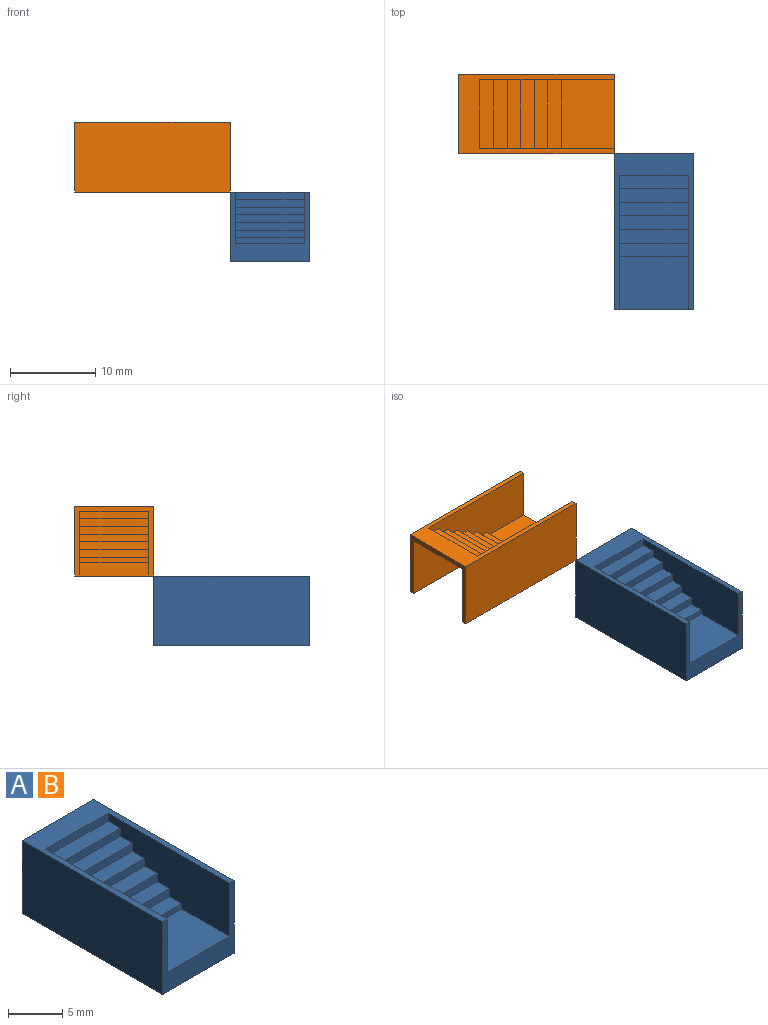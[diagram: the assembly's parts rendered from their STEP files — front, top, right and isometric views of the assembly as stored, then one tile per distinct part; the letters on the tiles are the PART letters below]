
ASSEMBLY  parts=2 mates=1
PART A: 40 faces, bbox 9.3x18.3x8.2 mm
  f0: plane 8.1x0.9mm, normal (0,-1,0), area 7.3mm2, adj f1,f33,f36,f37
  f1: plane 8.1x1.6mm, normal (0,0,1), area 13mm2, adj f0,f2,f36,f37
  f2: plane 8.1x0.9mm, normal (0,-1,0), area 7.3mm2, adj f1,f3,f36,f37
  f3: plane 8.1x1.6mm, normal (0,0,1), area 13mm2, adj f2,f4,f36,f37
  f4: plane 8.1x0.9mm, normal (0,-1,0), area 7.3mm2, adj f3,f5,f36,f37
  f5: plane 8.1x1.6mm, normal (0,0,1), area 13mm2, adj f4,f6,f36,f37
  f6: plane 8.1x0.9mm, normal (0,-1,0), area 7.3mm2, adj f5,f7,f36,f37
  f7: plane 8.1x1.6mm, normal (0,0,1), area 13mm2, adj f6,f8,f36,f37
  f8: plane 8.1x0.9mm, normal (0,-1,0), area 7.3mm2, adj f7,f9,f36,f37
  f9: plane 8.1x1.6mm, normal (0,0,1), area 13mm2, adj f8,f10,f36,f37
  f10: plane 8.1x0.9mm, normal (0,-1,0), area 7.3mm2, adj f9,f11,f36,f37
  f11: plane 8.1x1.6mm, normal (0,0,1), area 13mm2, adj f10,f12,f36,f37
  f12: plane 8.1x0.6mm, normal (0,-1,0), area 4.9mm2, adj f11,f13,f36,f37
  f13: plane 8.1x6.18mm, normal (0,0,1), area 50.1mm2, adj f12,f14,f36,f37
  f14: plane 9.3x8.2mm, normal (0,-1,0), area 27.7mm2, adj f13,f15,f33,f35,f36,f37,f39
  f15: plane 18.28x9.3mm, normal (0,0,-1), area 26.8mm2, adj f14,f16,f32,f34,f35,f38,f39
  f16: plane 8.1x1.6mm, normal (0,1,0), area 13mm2, adj f15,f17,f34,f38
  f17: plane 8.1x6.18mm, normal (0,0,-1), area 50.1mm2, adj f16,f18,f34,f38
  f18: plane 8.1x0.6mm, normal (0,1,0), area 4.9mm2, adj f17,f19,f34,f38
  f19: plane 8.1x1.6mm, normal (0,0,-1), area 13mm2, adj f18,f20,f34,f38
  f20: plane 8.1x0.9mm, normal (0,1,0), area 7.3mm2, adj f19,f21,f34,f38
  f21: plane 8.1x1.6mm, normal (0,0,-1), area 13mm2, adj f20,f22,f34,f38
  f22: plane 8.1x0.9mm, normal (0,1,0), area 7.3mm2, adj f21,f23,f34,f38
  f23: plane 8.1x1.6mm, normal (0,0,-1), area 13mm2, adj f22,f24,f34,f38
  f24: plane 8.1x0.9mm, normal (0,1,0), area 7.3mm2, adj f23,f25,f34,f38
  f25: plane 8.1x1.6mm, normal (0,0,-1), area 13mm2, adj f24,f26,f34,f38
  f26: plane 8.1x0.9mm, normal (0,1,0), area 7.3mm2, adj f25,f27,f34,f38
  f27: plane 8.1x1.6mm, normal (0,0,-1), area 13mm2, adj f26,f28,f34,f38
  f28: plane 8.1x0.9mm, normal (0,1,0), area 7.3mm2, adj f27,f29,f34,f38
  f29: plane 8.1x1.6mm, normal (0,0,-1), area 13mm2, adj f28,f30,f34,f38
  f30: plane 8.1x0.9mm, normal (0,1,0), area 7.3mm2, adj f29,f31,f34,f38
  f31: plane 8.1x1.9mm, normal (0,0,-1), area 15.4mm2, adj f30,f32,f34,f38
  f32: plane 9.3x8.2mm, normal (0,1,0), area 14.7mm2, adj f15,f31,f33,f34,f35,f38,f39
  f33: plane 18.28x9.3mm, normal (0,0,1), area 42.2mm2, adj f0,f14,f32,f35,f36,f37,f39
  f34: plane 17.68x7.6mm, normal (-1,0,0), area 67.1mm2, adj f15,f16,f17,f18,f19,f20,f21,f22
  f35: plane 18.28x8.2mm, normal (1,0,0), area 149.9mm2, adj f14,f15,f32,f33
  f36: plane 15.78x6mm, normal (-1,0,0), area 67.3mm2, adj f0,f1,f2,f3,f4,f5,f6,f7
  f37: plane 15.78x6mm, normal (1,0,0), area 67.3mm2, adj f0,f1,f2,f3,f4,f5,f6,f7
  f38: plane 17.68x7.6mm, normal (1,0,0), area 67.1mm2, adj f15,f16,f17,f18,f19,f20,f21,f22
  f39: plane 18.28x8.2mm, normal (-1,0,0), area 149.9mm2, adj f14,f15,f32,f33
PART B: same geometry as A
PLACE A t=(34.68,-2.47,-5.02)mm
PLACE B rot(axis=(0,0,1),90deg) t=(25.98,24.52,3.18)mm
MATE fastened A.f33 <-> B.f15  axis (0,0,1) through (25.98,15.82,3.18)mm
